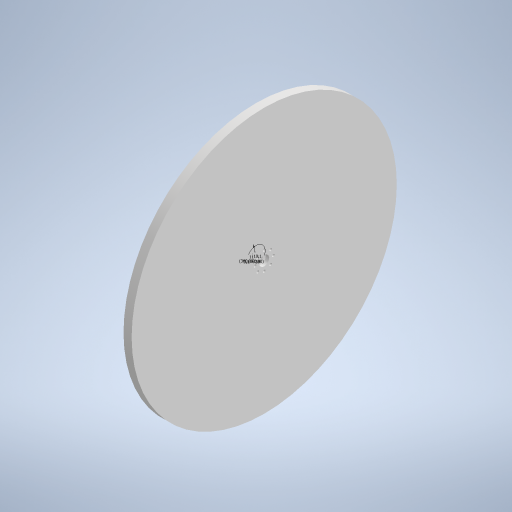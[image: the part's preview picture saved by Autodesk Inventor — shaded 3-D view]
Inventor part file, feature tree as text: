
AUTODESK INVENTOR PART (.ipt)
format: ipt  version: 2024.2 (Build 282272000, 272)  size: 262,656 bytes
history: native  units: mm
features: sketch x2, extrude x2, other x1, revolve x1
ambient origin geometry x8: Origin, YZ Plane, XZ Plane, XY Plane, X Axis, Y Axis, Z Axis, Center Point
bodies: Body1 (feature_tree)
feature tree (6):
  other  "Bryła1"
  revolve  "Obrót1"
  sketch  "Szkic2"
  extrude  "Wyciągnięcie proste1"  Depth=6.0mm
  extrude  "Wyciągnięcie proste2"  Depth=4.1mm
  sketch  "Szkic1"
